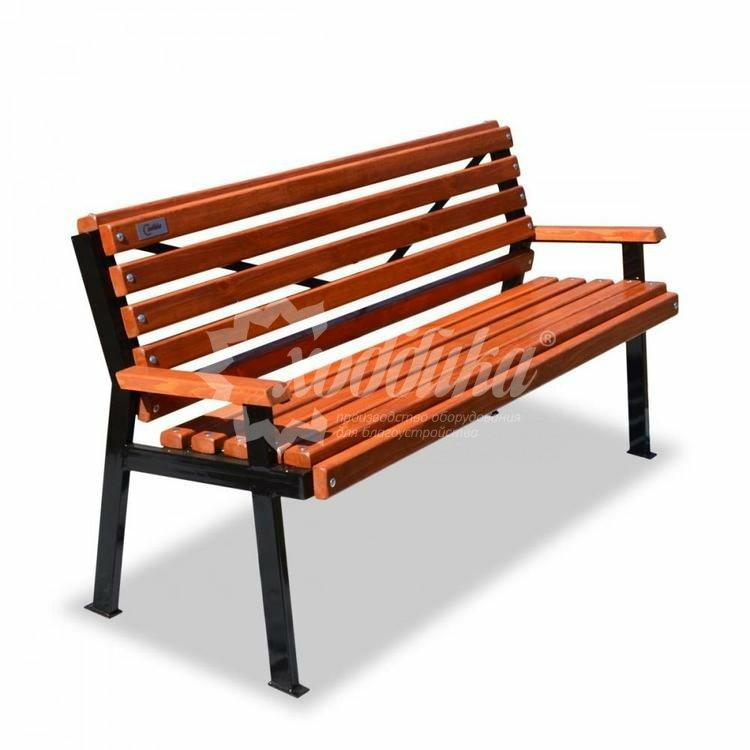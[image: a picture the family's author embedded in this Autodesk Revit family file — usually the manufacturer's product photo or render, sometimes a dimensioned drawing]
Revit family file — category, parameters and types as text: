
# Revit family: Скамейка стальная «Модерн» Арт 7106
name_source: partatom
category: Антураж
revit_build: Autodesk Revit 2018 (Build: 20180423_1000(x64)
units: mm (PartAtom-declared; Revit-internal decimal feet)

## family parameters
Всегда вертикально = Да
Источник визуального образа = Геометрия семейства
На основе рабочей плоскости = Нет
Общий = Нет
При загрузке вырезать с полостями = Нет
Точка расчета площади = Нет

## types (8) — shared parameters
URL = https://hobbyka.ru
Артикул товара = Арт. 7106
Высота = 835 мм
Группа модели = Садовые скамейки
Изготовитель = ООО «Хоббика»
Изображение типоразмера = Скамейка стальная «Модерн» Арт 7106.jpg
Цвет каркаса = Сталь
Цвет сидения = Дерево
Ширина = 612 мм

## per-type parameters (varying)
| type | Длина | Длина досок | Материал изделия | Модель 0,7 м (кресло) | Модель 1,2 м | Модель 1,5 м | Модель 1,5 м (композит) | Модель 1,8 м | Модель 1,8 м (композит) | Модель 2,0 м | Модель 3,0 м | Описание |
| Модель 0,7 м (кресло) | 820 мм | 744 мм | Сталь, дерево | Да | Нет | Нет | Нет | Нет | Нет | Нет | Нет | Скамейка стальная «Модерн». Модель 0,7 м (Кресло) |
| Модель 1,2 м | 1320 мм | 1244 мм | Сталь, дерево | Нет | Да | Нет | Нет | Нет | Нет | Нет | Нет | Скамейка стальная «Модерн». Модель 1,2 м |
| Модель 1,5 м | 1620 мм | 1544 мм | Сталь, дерево | Нет | Нет | Да | Нет | Нет | Нет | Нет | Нет | Скамейка стальная «Модерн». Модель 1,5 м |
| Модель 1,8 м | 1920 мм | 1844 мм | Сталь, дерево | Нет | Нет | Нет | Нет | Да | Нет | Нет | Нет | Скамейка стальная «Модерн». Модель 1,8 м |
| Модель 2,0 м | 2120 мм | 2044 мм | Сталь, дерево | Нет | Нет | Нет | Нет | Нет | Нет | Да | Нет | Скамейка стальная «Модерн». Модель 2,0 м. С тремя опорами |
| Модель 3,0 м | 3120 мм | 3044 мм | Сталь, дерево | Нет | Нет | Нет | Нет | Нет | Нет | Нет | Да | Скамейка стальная «Модерн». Модель 3,0 м. С тремя опорами |
| Модель 1,5 м (композит) | 1620 мм | 1544 мм | Сталь, композитный материал | Нет | Нет | Нет | Да | Нет | Нет | Нет | Нет | Скамейка стальная «Модерн». Модель 1,5 м. Сидение из композитных материалов |
| Модель 1,8 м (композит) | 1920 мм | 1844 мм | Сталь, композитный материал | Нет | Нет | Нет | Нет | Нет | Да | Нет | Нет | Скамейка стальная «Модерн». Модель 1,8 м. Сидение из композитных материалов |
